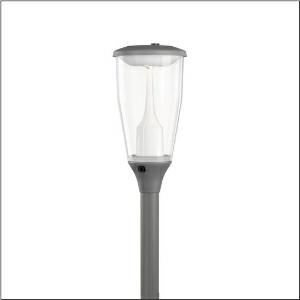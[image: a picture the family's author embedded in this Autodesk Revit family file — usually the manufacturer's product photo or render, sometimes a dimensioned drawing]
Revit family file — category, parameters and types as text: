
# Revit family: dl_11_iq___st1_2a_5xa5575ew14hp00022_a9c4
name_source: partatom
category: Lighting Fixtures
units: mm (PartAtom-declared; Revit-internal decimal feet)

## family parameters
Cut with Voids When Loaded = No
Host = Face
Light Source = No
Part Type = Normal
Room Calculation Point = No
Round Connector Dimension = Use Diameter
Shared = No

## types (1)
- --- (1 x LED, 4790 lm, 33.5 W, 3000K)
    Apparent Load = 34 VA
    CIE Flux Codes = 23 60 93 95 100
    Color Rendering = 70
    Color Temperature = 3000K
    Default Elevation = 1800 mm
    Description = DL 11 iQ, mast luminaire, Module 540 iQ-SR, primary light control with 3 zone facetted reflector, of plastic, silver coated, highly specular, structured, primary optical cover: cover, of PMMA, transparent, light distribution: ST1.2a, light emission: direct distribution, primary light characteristic: asymmetric, installation type: post-top, LED, High Power LED, rated luminous flux: 4.790lm, luminous efficacy: 143lm/W, light colour: 730, colour temperature: 3000K, control gear: iQ-Street Remote, D4i with power reduction, control: pre-setting: logarithmic dimming characteristic, Street-Remote, Auto-Match, Temp-Guard, Lumen-Switch, Night-Set, Smart-Wire, Light-Fading, Desk-Remote (wireless, voltage-free reading and setting of iQ features in the workshop via application-optimized NFC function/RFID function), optimised constant luminous flux control (CLO 2.0), mains connection: 220..240V, AC, 50/60Hz, connection cable pre-assembled, cable length: 5,5m, start of lifetime: 34W, end of service life: 36W, reduction: 15W, luminaire housing, upper part, of diecast aluminium, coated, Siteco® metallic grey (DB 702S), spigot size: 76mm (post-top), mounting height: 3..5m, post-top mast mounting element, of diecast aluminium, coated, Siteco® metallic grey (DB 702S), Module 540 iQ-SR, traffic white (RAL 9016), equipment: Power, Smart Interface above and design motion detector below, protection rating (complete): IP65, insulation class (complete): insulation class II (safety insulation), certification: CE, ENEC, ENEC+, VDE, impact resistance: IK07, packaging unit: 1 piece

Light Distribution: ST1.2a
    Height = 665 mm
    Lamp = 1 x LED
    Lamp Light Flux = 4790 lm
    Lamp Power = 33.5 W
    Lamp count = 1
    Length = 334 mm
    Luminous efficacy = 143 lm/W
    Manufacturer = Siteco
    ModVariant = No
    Model = 5XA5575EW14HP00022
    Number of Poles = 1
    OnlyDefault = Yes
    Power Factor = 1
    Product Name = DL 11 iQ | ST1.2a
    Product group = mast luminaire | pylon top
    ProductGroupID = 6100
    Protection Class = Protection class II
    Protection Degree = IP 65
    RLX_Detail_Level = 1
    RLX_Emergency_Light_Flux = 0 lm
    RLX_Emergency_Type = 0
    RLX_Emergency_Type_DB = No
    RlxData = <blob elided: 160829 chars, md5=aa9a40e1>
    Socket = socket
    Standby Power = 0 W
    System Light Flux = 4790 lm
    System Power = 34 W
    Type Comments = factory setting: luminous flux: 100 % | dim-lin: 254 | 695 mA
    Type Image = l_1337543.jpg
    URL = http://relux.com
    VarID = @adj_033778
    Voltage = 0 V
    Weight = 0.00 kg
    Width = 0 mm  [stored 0 ft]

note: [stored X ft] marks values corroborated as IEEE doubles in the binary element streams (Revit-internal decimal feet)

## geometry (parser evidence)
native form markers: Blend x4, Sweep x11
no freeform markers — native parametric forms only
